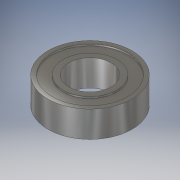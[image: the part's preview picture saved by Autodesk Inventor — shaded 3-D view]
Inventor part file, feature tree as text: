
AUTODESK INVENTOR PART (.ipt)
format: ipt  version: 2019 (Build 230136000, 136)  size: 134,144 bytes
history: native  units: mm
features: revolve x1, sketch x1
ambient origin geometry x8: Origin, YZ Plane, XZ Plane, XY Plane, X Axis, Y Axis, Z Axis, Center Point
bodies: Solid1 (feature_tree)
feature tree (2):
  revolve  "Revolution1"  [1 undecoded]
  sketch  "Sketch1"  dims[d0=90.0deg]
note: 1 required parameter value undecoded (feature->parameter linkage not recoverable at this tier; creation-order binding heuristic only, values carry confidence <= 0.55)
